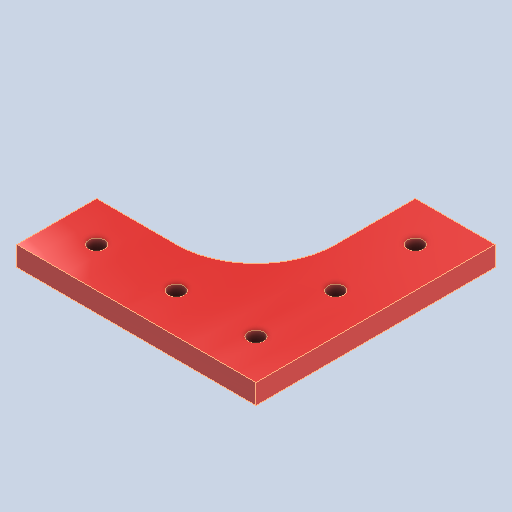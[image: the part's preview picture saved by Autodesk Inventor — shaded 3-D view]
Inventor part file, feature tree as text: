
AUTODESK INVENTOR PART (.ipt)
format: ipt  version: 2023 (Build 270158000, 158)  size: 265,728 bytes
history: native  units: in
note: dims shown in document units (in); Inventor stores cm internally (conversion verified against a paired STEP export)
features: extrude x1, sketch x1
ambient origin geometry x8: Origin, YZ Plane, XZ Plane, XY Plane, X Axis, Y Axis, Z Axis, Center Point
bodies: Solid1 (feature_tree)
feature tree (2):
  extrude  "Extrusion1"  Depth=1.0in
  sketch  "Sketch1"  dims[d0=3.0in d1=1.0in d2=1.0in d3=3.0in d4=1.0in d5=0.1969in d6=0.1969in d7=0.1969in d8=0.1969in d9=0.1969in d10=0.5in d11=0.5in d12=0.5in d13=0.5in d14=0.5in d15=0.5in d16=1.5in d17=1.5in d18=0.5in d19=0.5in d20=0.25in d21=0.0in]
